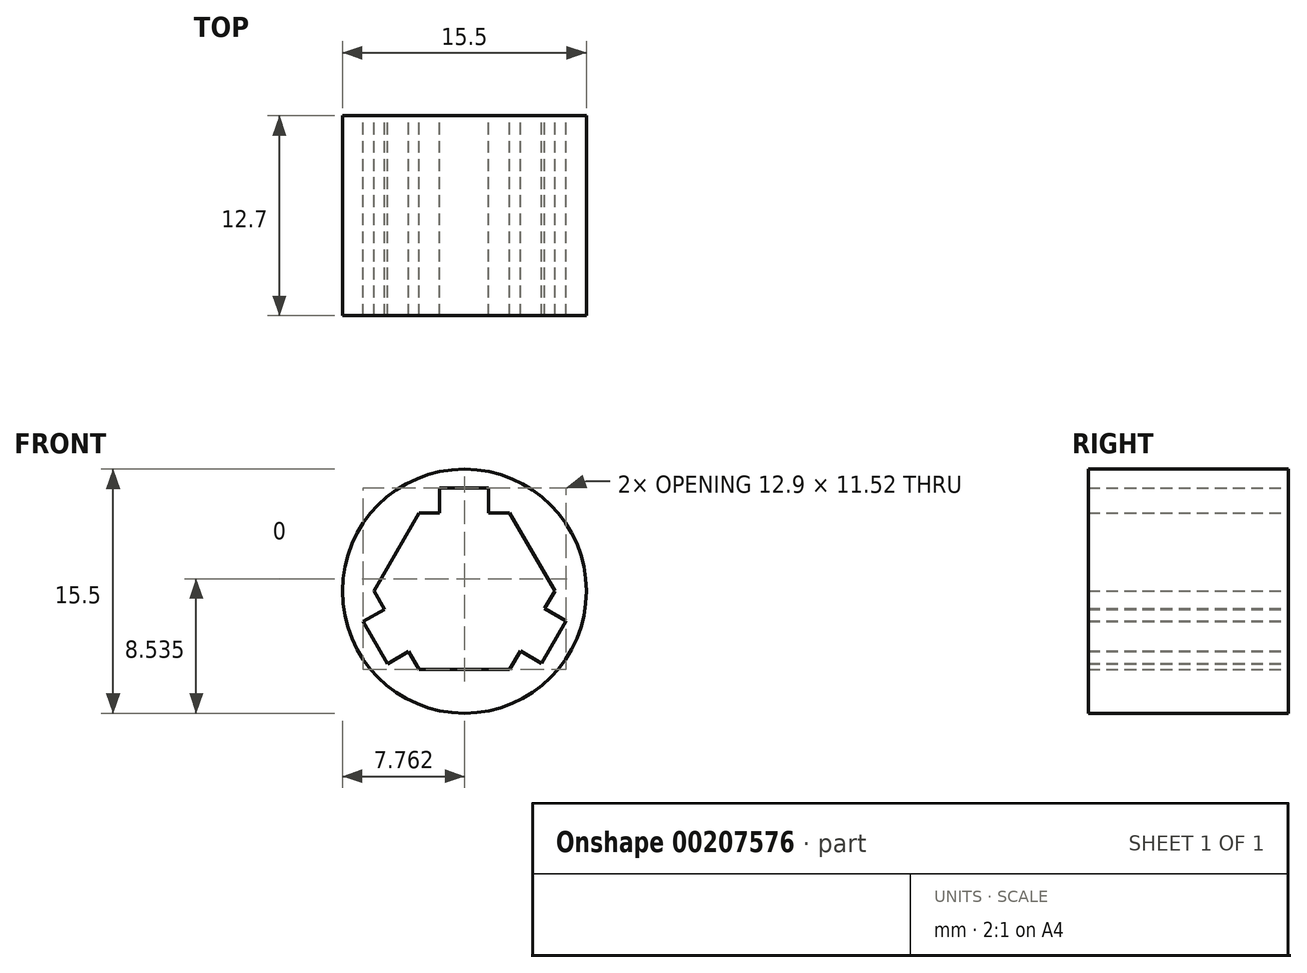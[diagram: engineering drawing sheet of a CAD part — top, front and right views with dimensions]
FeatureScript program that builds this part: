
annotation { "Feature Type Name" : "Feature", "Feature Type Description" : "" }
export const myFeature = defineFeature(function(context is Context, id is Id, definition is map)
    precondition{}
    {
        {
            var Q0;
            Q0=qCreatedBy(makeId("Front.planeOp"),FACE);
            var sketch = newSketch(context, id + "F0", { "sketchPlane" : qUnion([Q0])});
            skCircle(sketch, "E0.cCircle", {"center": v(0, 0) * mm, "radius": 4.97 * mm, "construction": true});
            skLineSegment(sketch, "E0.0", {"start": v(5.74, 0) * mm, "end": v(2.87, -4.98) * mm});
            skLineSegment(sketch, "E0.1", {"start": v(2.87, -4.97) * mm, "end": v(-2.87, -4.97) * mm});
            skLineSegment(sketch, "E0.2", {"start": v(-2.87, -4.97) * mm, "end": v(-5.74, 0) * mm});
            skLineSegment(sketch, "E0.3", {"start": v(-5.74, 0) * mm, "end": v(-2.87, 4.98) * mm});
            skLineSegment(sketch, "E0.4", {"start": v(-2.87, 4.97) * mm, "end": v(2.87, 4.97) * mm});
            skLineSegment(sketch, "E0.5", {"start": v(2.87, 4.97) * mm, "end": v(5.74, 0) * mm});
            skPoint(sketch, "E0.0.midPoint", {"position": v(4.3, -2.49) * mm});
            skLineSegment(sketch, "E1", {"start": v(0, 4.97) * mm, "end": v(0, -4.97) * mm, "construction": true});
            skCircle(sketch, "E2", {"center": v(0, 0) * mm, "radius": 7.75 * mm});
            skLineSegment(sketch, "E3", {"start": v(-5.74, 0) * mm, "end": v(5.74, 0) * mm, "construction": true});
            skLineSegment(sketch, "E4", {"start": v(-1.56, 6.54) * mm, "end": v(1.54, 6.54) * mm});
            skLineSegment(sketch, "E5", {"start": v(1.54, 6.54) * mm, "end": v(1.54, 4.97) * mm});
            skLineSegment(sketch, "E6", {"start": v(-1.56, 6.54) * mm, "end": v(-1.56, 4.97) * mm});
            skPoint(sketch, "E7", {"position": v(-0.01, 6.54) * mm});
            skLineSegment(sketch, "E8", {"start": v(-0.01, 6.54) * mm, "end": v(0, 4.97) * mm, "construction": true});
            skLineSegment(sketch, "E9", {"start": v(-5.08, -1.15) * mm, "end": v(-6.44, -1.94) * mm});
            skLineSegment(sketch, "E10", {"start": v(-6.44, -1.94) * mm, "end": v(-4.89, -4.62) * mm});
            skLineSegment(sketch, "E11", {"start": v(-4.89, -4.62) * mm, "end": v(-3.53, -3.84) * mm});
            skPoint(sketch, "E12", {"position": v(-5.66, -3.28) * mm});
            skPoint(sketch, "E13", {"position": v(-4.3, -2.49) * mm});
            skLineSegment(sketch, "E14", {"start": v(-5.66, -3.28) * mm, "end": v(-4.3, -2.49) * mm, "construction": true});
            skLineSegment(sketch, "E15", {"start": v(3.55, -3.8) * mm, "end": v(4.91, -4.58) * mm});
            skLineSegment(sketch, "E16", {"start": v(4.91, -4.58) * mm, "end": v(6.46, -1.9) * mm});
            skLineSegment(sketch, "E17", {"start": v(6.46, -1.9) * mm, "end": v(5.1, -1.1) * mm});
            skPoint(sketch, "E18", {"position": v(5.69, -3.24) * mm});
            skSolve(sketch);
        }
        {
            var Q0;
            Q0=makeQuery(id+"F0.imprint","IMPRINT",FACE,{"disambiguationData":[TD([[makeQuery(id+"F0.imprint","IMPRINT",EDGE,{"derivedFrom":sQuery(id+"F0.wireOp",EDGE,"E0.0")}),1.0]])]});
            extrude(context, id + "F1", {"entities" : qUnion([Q0]), "depth" : 12.7 * mm, "offsetDistance" : 25 * mm});
        }
        {
            var Q0;
            Q0=makeQuery(id+"F1.opExtrude","SWEPT_BODY",BODY,{"disambiguationData":[OSD([sQuery(id+"F0.wireOp",EDGE,"E0.0"),sQuery(id+"F0.wireOp",EDGE,"E0.1"),sQuery(id+"F0.wireOp",EDGE,"E0.2"),sQuery(id+"F0.wireOp",EDGE,"E0.3"),sQuery(id+"F0.wireOp",EDGE,"E0.4"),sQuery(id+"F0.wireOp",EDGE,"E0.5"),sQuery(id+"F0.wireOp",EDGE,"E2")])]});
            transform(context, id + "F2", {"entities" : qUnion([Q0]), "transformType" : TransformType.TRANSLATION_3D, "dx" : 0 * mm, "dy" : 0 * mm, "dz" : 0 * mm, "makeCopy" : true});
        }
    });
